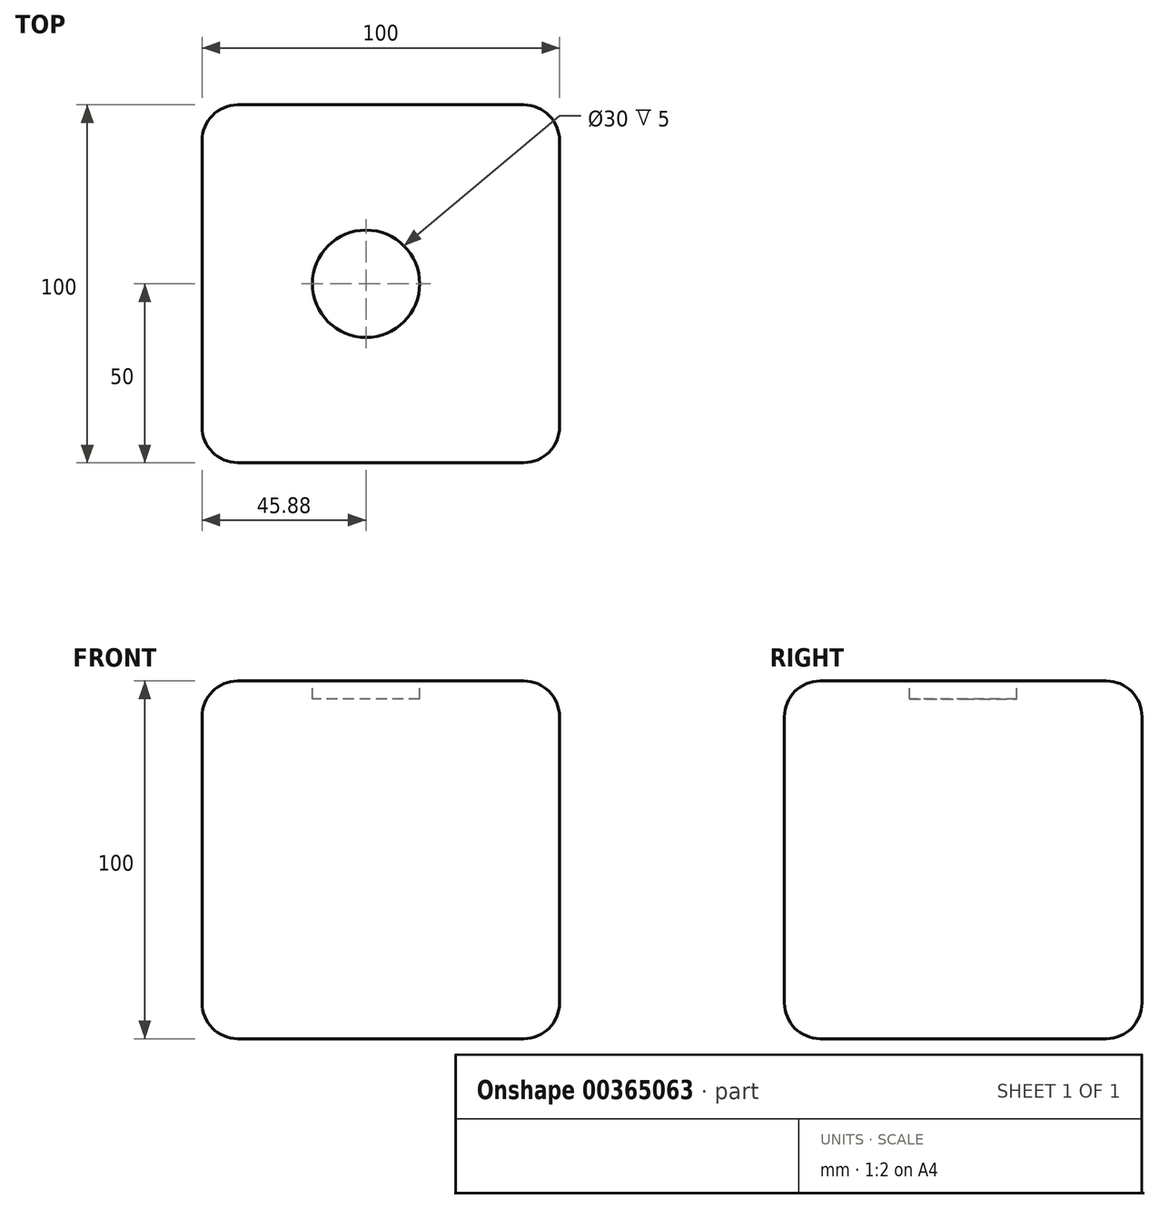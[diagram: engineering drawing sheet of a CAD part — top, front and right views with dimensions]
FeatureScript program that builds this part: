
annotation { "Feature Type Name" : "Feature", "Feature Type Description" : "" }
export const myFeature = defineFeature(function(context is Context, id is Id, definition is map)
    precondition{}
    {
        {
            var Q0;
            Q0=qCreatedBy(makeId("Top.planeOp"),FACE);
            var sketch = newSketch(context, id + "F0", { "sketchPlane" : qUnion([Q0])});
            skLineSegment(sketch, "E0.bottom", {"start": v(-45.88, 50) * mm, "end": v(54.12, 50) * mm});
            skLineSegment(sketch, "E0.top", {"start": v(-45.88, -50) * mm, "end": v(54.12, -50) * mm});
            skLineSegment(sketch, "E0.left", {"start": v(-45.88, 50) * mm, "end": v(-45.88, -50) * mm});
            skLineSegment(sketch, "E0.right", {"start": v(54.12, 50) * mm, "end": v(54.12, -50) * mm});
            skPoint(sketch, "E1", {"position": v(4.12, -50) * mm});
            skPoint(sketch, "E2", {"position": v(-45.88, 0) * mm});
            skSolve(sketch);
        }
        {
            var Q0;
            Q0 = qSketchRegion(id + "F0", true);
            extrude(context, id + "F1", {"entities" : qUnion([Q0]), "depth" : 100 * mm});
        }
        {
            var Q0;
            Q0=makeQuery(id+"F1.opExtrude","CAP_FACE",FACE,{"disambiguationData":[OSD([sQuery(id+"F0.wireOp",EDGE,"E0.bottom"),sQuery(id+"F0.wireOp",EDGE,"E0.top"),sQuery(id+"F0.wireOp",EDGE,"E0.left"),sQuery(id+"F0.wireOp",EDGE,"E0.right")])],"isStart":false});
            var Q1;
            Q1=makeQuery(id+"F1.opExtrude","SWEPT_FACE",FACE,{"disambiguationData":[OSD([sQuery(id+"F0.wireOp",EDGE,"E0.top")])]});
            var Q2;
            Q2=makeQuery(id+"F1.opExtrude","SWEPT_FACE",FACE,{"disambiguationData":[OSD([sQuery(id+"F0.wireOp",EDGE,"E0.right")])]});
            var Q3;
            Q3=makeQuery(id+"F1.opExtrude","SWEPT_FACE",FACE,{"disambiguationData":[OSD([sQuery(id+"F0.wireOp",EDGE,"E0.bottom")])]});
            var Q4;
            Q4=makeQuery(id+"F1.opExtrude","SWEPT_FACE",FACE,{"disambiguationData":[OSD([sQuery(id+"F0.wireOp",EDGE,"E0.left")])]});
            fillet(context, id + "F2", {"entities" : qUnion([Q0, Q1, Q2, Q3, Q4]), "radius" : 10 * mm, "tangentPropagation" : true, "allowEdgeOverflow" : false});
        }
        {
            var Q0;
            Q0=makeQuery(id+"F1.opExtrude","CAP_FACE",FACE,{"disambiguationData":[OSD([sQuery(id+"F0.wireOp",EDGE,"E0.bottom"),sQuery(id+"F0.wireOp",EDGE,"E0.top"),sQuery(id+"F0.wireOp",EDGE,"E0.left"),sQuery(id+"F0.wireOp",EDGE,"E0.right")])],"isStart":false});
            var sketch = newSketch(context, id + "F3", { "sketchPlane" : qUnion([Q0])});
            skCircle(sketch, "E3", {"center": v(0, 0) * mm, "radius": 15 * mm});
            skSolve(sketch);
        }
        {
            var Q0;
            Q0=makeQuery(id+"F3.imprint","IMPRINT",FACE,{"disambiguationData":[TD([[makeQuery(id+"F3.imprint","IMPRINT",EDGE,{"derivedFrom":sQuery(id+"F3.wireOp",EDGE,"E3")}),1.0]])]});
            extrude(context, id + "F4", {"entities" : qUnion([Q0]), "operationType" : NewBodyOperationType.REMOVE, "oppositeDirection" : true, "depth" : 5 * mm});
        }
    });
